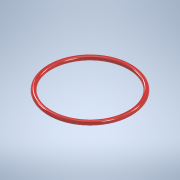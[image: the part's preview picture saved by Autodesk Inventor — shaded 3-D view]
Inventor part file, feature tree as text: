
AUTODESK INVENTOR PART (.ipt)
format: ipt  version: 2020 (Build 240168000, 168)  size: 139,776 bytes
history: native  units: mm
features: sketch x3, plane x2, revolve x1
ambient origin geometry x8: Origin, YZ Plane, XZ Plane, XY Plane, X Axis, Y Axis, Z Axis, Center Point
bodies: Solid1 (feature_tree)
feature tree (6):
  revolve  "Revolution1"  [1 undecoded]
  plane  "Work Plane2"
  sketch  "Sketch2"  dims[d2=90.0deg]
  sketch  "Sketch3"  dims[d3=2.665mm d4=-5.33mm d5=94.0mm d6=90.0mm]
  sketch  "Sketch1"  dims[d0=5.33mm d1=49.975mm]
  plane  "Work Plane1"
note: 1 required parameter value undecoded (feature->parameter linkage not recoverable at this tier; creation-order binding heuristic only, values carry confidence <= 0.55)
